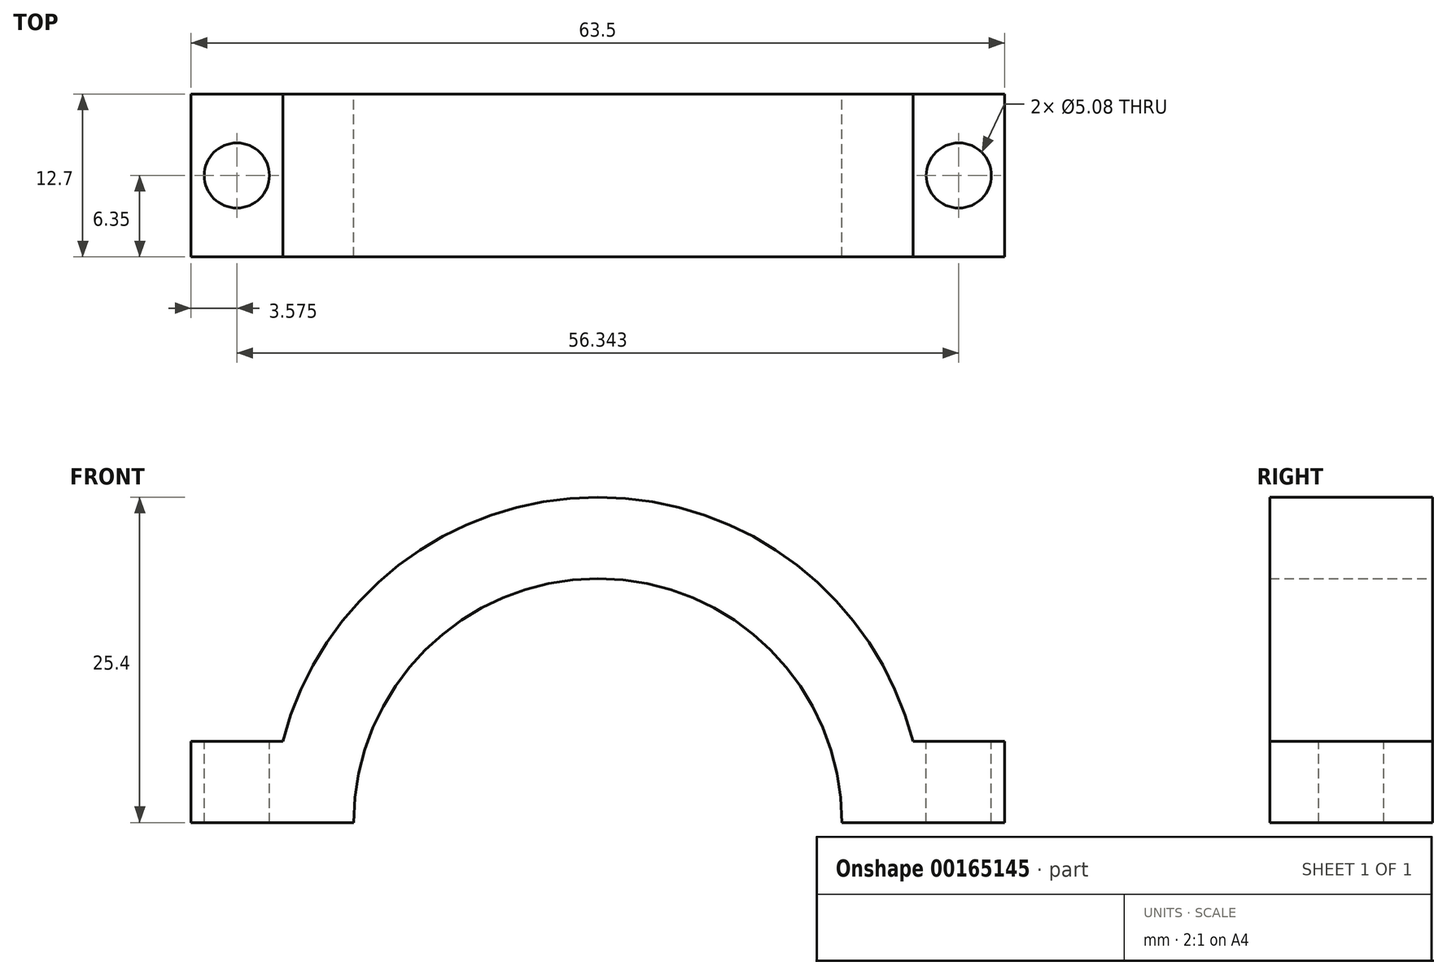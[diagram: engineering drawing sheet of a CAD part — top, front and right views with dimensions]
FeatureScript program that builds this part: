
annotation { "Feature Type Name" : "Feature", "Feature Type Description" : "" }
export const myFeature = defineFeature(function(context is Context, id is Id, definition is map)
    precondition{}
    {
        {
            var Q0;
            Q0=qCreatedBy(makeId("Front.planeOp"),FACE);
            var sketch = newSketch(context, id + "F0", { "sketchPlane" : qUnion([Q0])});
            skArc(sketch, "E0", {"start": v(-49.85, 22.34) * mm, "mid": v(-68.9, 41.39) * mm, "end": v(-87.95, 22.34) * mm});
            skArc(sketch, "E1", {"start": v(-43.5, 22.34) * mm, "mid": v(-68.9, 47.74) * mm, "end": v(-94.3, 22.34) * mm});
            skLineSegment(sketch, "E2", {"start": v(-94.3, 22.34) * mm, "end": v(-87.95, 22.34) * mm});
            skLineSegment(sketch, "E3", {"start": v(-49.85, 22.34) * mm, "end": v(-43.5, 22.34) * mm});
            skLineSegment(sketch, "E4.bottom", {"start": v(-49.85, 22.34) * mm, "end": v(-37.15, 22.34) * mm});
            skLineSegment(sketch, "E4.top", {"start": v(-49.85, 28.69) * mm, "end": v(-37.15, 28.69) * mm});
            skLineSegment(sketch, "E4.left", {"start": v(-49.85, 22.34) * mm, "end": v(-49.85, 28.69) * mm});
            skLineSegment(sketch, "E4.right", {"start": v(-37.15, 22.34) * mm, "end": v(-37.15, 28.69) * mm});
            skLineSegment(sketch, "E5.bottom", {"start": v(-87.95, 22.34) * mm, "end": v(-100.65, 22.34) * mm});
            skLineSegment(sketch, "E5.top", {"start": v(-87.95, 28.69) * mm, "end": v(-100.65, 28.69) * mm});
            skLineSegment(sketch, "E5.left", {"start": v(-87.95, 22.34) * mm, "end": v(-87.95, 28.69) * mm});
            skLineSegment(sketch, "E5.right", {"start": v(-100.65, 22.34) * mm, "end": v(-100.65, 28.69) * mm});
            skSolve(sketch);
        }
        {
            var Q0;
            Q0 = qSketchRegion(id + "F0", true);
            extrude(context, id + "F1", {"entities" : qUnion([Q0]), "depth" : 12.7 * mm});
        }
        {
            var Q0;
            Q0=makeQuery(id+"F1.opExtrude","SWEPT_FACE",FACE,{"disambiguationData":[OSD([sQuery(id+"F0.wireOp",EDGE,"E4.top")])]});
            var sketch = newSketch(context, id + "F2", { "sketchPlane" : qUnion([Q0])});
            skCircle(sketch, "E6", {"center": v(-40.73, -6.35) * mm, "radius": 2.54 * mm});
            skPoint(sketch, "E6.centerSnap0", {"position": v(-37.15, -6.35) * mm});
            skPoint(sketch, "E6.centerSnap1", {"position": v(-40.73, -12.7) * mm});
            skSolve(sketch);
        }
        {
            var Q0;
            Q0=makeQuery(id+"F2.imprint","IMPRINT",FACE,{"disambiguationData":[TD([[makeQuery(id+"F2.imprint","IMPRINT",EDGE,{"derivedFrom":sQuery(id+"F2.wireOp",EDGE,"E6")}),1.0]])]});
            extrude(context, id + "F3", {"entities" : qUnion([Q0]), "operationType" : NewBodyOperationType.REMOVE, "oppositeDirection" : true, "depth" : 25.4 * mm});
        }
        {
            var Q0;
            Q0=makeQuery(id+"F1.opExtrude","SWEPT_FACE",FACE,{"disambiguationData":[OSD([sQuery(id+"F0.wireOp",EDGE,"E5.top")])]});
            var sketch = newSketch(context, id + "F4", { "sketchPlane" : qUnion([Q0])});
            skCircle(sketch, "E7", {"center": v(-97.08, -6.35) * mm, "radius": 2.54 * mm});
            skPoint(sketch, "E7.centerSnap0", {"position": v(-100.65, -6.35) * mm});
            skPoint(sketch, "E7.centerSnap1", {"position": v(-97.08, -12.7) * mm});
            skSolve(sketch);
        }
        {
            var Q0;
            Q0 = qSketchRegion(id + "F4", true);
            extrude(context, id + "F5", {"entities" : qUnion([Q0]), "operationType" : NewBodyOperationType.REMOVE, "oppositeDirection" : true, "depth" : 25.4 * mm});
        }
    });
